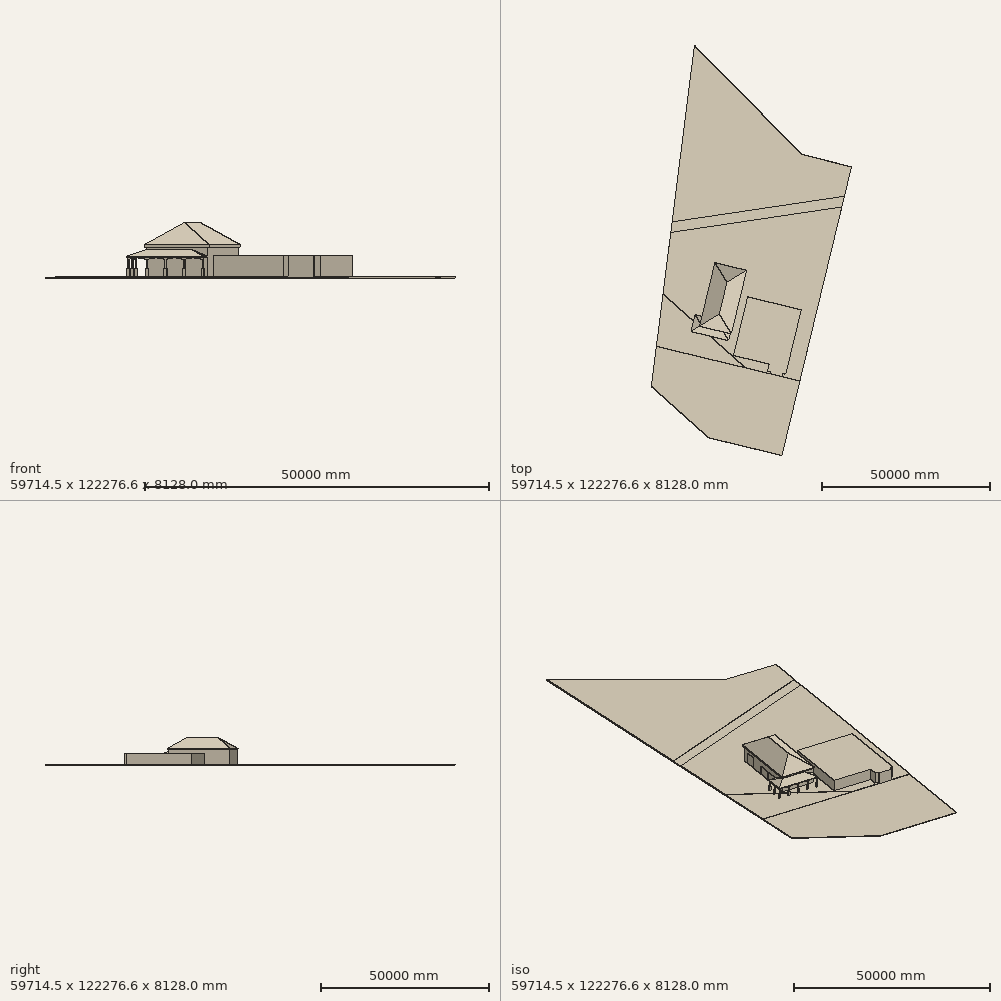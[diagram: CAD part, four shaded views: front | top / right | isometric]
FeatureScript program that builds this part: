
annotation { "Feature Type Name" : "Feature", "Feature Type Description" : "" }
export const myFeature = defineFeature(function(context is Context, id is Id, definition is map)
    precondition{}
    {
        {
            var Q0;
            Q0=qCreatedBy(makeId("Top.planeOp"),FACE);
            var sketch = newSketch(context, id + "F0", { "sketchPlane" : qUnion([Q0])});
            skLineSegment(sketch, "E0", {"start": v(0, 0) * mm, "end": v(31989.83, -32467.96) * mm});
            skLineSegment(sketch, "E1", {"start": v(31989.83, -32467.96) * mm, "end": v(46862.18, -36229.17) * mm});
            skLineSegment(sketch, "E2", {"start": v(46862.18, -36229.17) * mm, "end": v(26112.23, -122276.56) * mm});
            skLineSegment(sketch, "E3", {"start": v(46862.18, -36229.17) * mm, "end": v(46862.18, -51469.17) * mm, "construction": true});
            skLineSegment(sketch, "E4", {"start": v(0, 0) * mm, "end": v(-12852.3, -101676.89) * mm});
            skLineSegment(sketch, "E5", {"start": v(0, 0) * mm, "end": v(0, 15240) * mm, "construction": true});
            skLineSegment(sketch, "E6", {"start": v(26112.23, -122276.56) * mm, "end": v(4230, -116999.76) * mm});
            skLineSegment(sketch, "E7", {"start": v(26112.23, -122276.56) * mm, "end": v(10872.23, -122276.56) * mm, "construction": true});
            skLineSegment(sketch, "E8", {"start": v(4230, -116999.76) * mm, "end": v(-12852.3, -101676.89) * mm});
            skArc(sketch, "E9", {"start": v(-4165.07, -109469.35) * mm, "mid": v(-689.73, -114039.67) * mm, "end": v(4230, -116999.76) * mm, "construction": true});
            skArc(sketch, "E10", {"start": v(-4165.07, -109469.35) * mm, "mid": v(-8132.26, -105153.47) * mm, "end": v(-12852.3, -101676.89) * mm, "construction": true});
            skLineSegment(sketch, "E11", {"start": v(31471.2, -100053.58) * mm, "end": v(-11342.08, -89729.35) * mm});
            skLineSegment(sketch, "E12", {"start": v(-9365.85, -74095.03) * mm, "end": v(15198.72, -96129.54) * mm});
            skLineSegment(sketch, "E13", {"start": v(-6651.63, -52622.31) * mm, "end": v(44754.67, -44968.73) * mm});
            skLineSegment(sketch, "E14", {"start": v(-7048.63, -55763.02) * mm, "end": v(43983.88, -48165.09) * mm});
            skSolve(sketch);
        }
        {
            var Q0;
            {var subQ4=sQuery(id+"F0.wireOp",EDGE,"E0");Q0=makeQuery(id+"F0.imprint","IMPRINT",FACE,{"disambiguationData":[TD([[makeQuery(id+"F0.imprint","IMPRINT",EDGE,{"derivedFrom":subQ4}),-1.0]])]});}
            var Q1;
            {var subQ0=sQuery(id+"F0.wireOp",EDGE,"E13");Q1=makeQuery(id+"F0.imprint","IMPRINT",FACE,{"disambiguationData":[TD([[makeQuery(id+"F0.imprint","IMPRINT",EDGE,{"derivedFrom":subQ0}),-1.0]])]});}
            var Q2;
            {var subQ0=sQuery(id+"F0.wireOp",EDGE,"E12");Q2=makeQuery(id+"F0.imprint","IMPRINT",FACE,{"disambiguationData":[TD([[makeQuery(id+"F0.imprint","IMPRINT",EDGE,{"derivedFrom":subQ0}),1.0]])]});}
            var Q3;
            {var subQ3=sQuery(id+"F0.wireOp",EDGE,"E12");Q3=makeQuery(id+"F0.imprint","IMPRINT",FACE,{"disambiguationData":[TD([[makeQuery(id+"F0.imprint","IMPRINT",EDGE,{"derivedFrom":subQ3}),-1.0]])]});}
            var Q4;
            {var subQ1=sQuery(id+"F0.wireOp",EDGE,"E6");Q4=makeQuery(id+"F0.imprint","IMPRINT",FACE,{"disambiguationData":[TD([[makeQuery(id+"F0.imprint","IMPRINT",EDGE,{"derivedFrom":subQ1}),-1.0]])]});}
            extrude(context, id + "F1", {"entities" : qUnion([Q0, Q1, Q2, Q3, Q4]), "depth" : 304.8 * mm, "offsetDistance" : 25.4 * mm});
        }
        {
            var Q0;
            Q0=makeQuery(id+"F1.opExtrude","CAP_FACE",FACE,{"disambiguationData":[OSD([sQuery(id+"F0.wireOp",EDGE,"E0"),sQuery(id+"F0.wireOp",EDGE,"E1"),sQuery(id+"F0.wireOp",EDGE,"E2"),sQuery(id+"F0.wireOp",EDGE,"E4"),sQuery(id+"F0.wireOp",EDGE,"E6"),sQuery(id+"F0.wireOp",EDGE,"E8")])],"isStart":false});
            var sketch = newSketch(context, id + "F2", { "sketchPlane" : qUnion([Q0])});
            skLineSegment(sketch, "E15.0", {"start": v(-9365.85, -74095.03) * mm, "end": v(15198.72, -96129.54) * mm});
            skLineSegment(sketch, "E16.0", {"start": v(31471.2, -100053.58) * mm, "end": v(-11342.08, -89729.35) * mm});
            skLineSegment(sketch, "E17.0", {"start": v(0, 0) * mm, "end": v(-12852.3, -101676.89) * mm});
            skSolve(sketch);
        }
        {
            var Q0;
            {var subQ0=sQuery(id+"F2.wireOp",EDGE,"E15.0");Q0=makeQuery(id+"F2.imprint","IMPRINT",FACE,{"disambiguationData":[TD([[makeQuery(id+"F2.imprint","IMPRINT",EDGE,{"derivedFrom":subQ0}),-1.0]])]});}
            extrude(context, id + "F3", {"entities" : qUnion([Q0]), "operationType" : NewBodyOperationType.REMOVE, "oppositeDirection" : true, "depth" : 76.2 * mm, "offsetDistance" : 25.4 * mm});
        }
        {
            var Q0;
            Q0=makeQuery(id+"F1.opExtrude","CAP_FACE",FACE,{"disambiguationData":[OSD([sQuery(id+"F0.wireOp",EDGE,"E0"),sQuery(id+"F0.wireOp",EDGE,"E1"),sQuery(id+"F0.wireOp",EDGE,"E2"),sQuery(id+"F0.wireOp",EDGE,"E4"),sQuery(id+"F0.wireOp",EDGE,"E6"),sQuery(id+"F0.wireOp",EDGE,"E8")])],"isStart":false});
            var sketch = newSketch(context, id + "F4", { "sketchPlane" : qUnion([Q0])});
            skLineSegment(sketch, "E18.0", {"start": v(0, 0) * mm, "end": v(-12852.3, -101676.89) * mm});
            skLineSegment(sketch, "E19.0", {"start": v(4230, -116999.76) * mm, "end": v(-12852.3, -101676.89) * mm});
            skLineSegment(sketch, "E20.0", {"start": v(26112.23, -122276.56) * mm, "end": v(4230, -116999.76) * mm});
            skLineSegment(sketch, "E21.0", {"start": v(46862.18, -36229.17) * mm, "end": v(26112.23, -122276.56) * mm});
            skLineSegment(sketch, "E22.0", {"start": v(31471.2, -100053.58) * mm, "end": v(-11342.08, -89729.35) * mm});
            skSolve(sketch);
        }
        {
            var Q0;
            {var subQ4=sQuery(id+"F4.wireOp",EDGE,"E19.0");Q0=makeQuery(id+"F4.imprint","IMPRINT",FACE,{"disambiguationData":[TD([[makeQuery(id+"F4.imprint","IMPRINT",EDGE,{"derivedFrom":subQ4}),-1.0]])]});}
            extrude(context, id + "F5", {"entities" : qUnion([Q0]), "operationType" : NewBodyOperationType.REMOVE, "oppositeDirection" : true, "depth" : 152.4 * mm, "offsetDistance" : 25.4 * mm});
        }
        {
            var Q0;
            Q0=makeQuery(id+"F1.opExtrude","CAP_FACE",FACE,{"disambiguationData":[OSD([sQuery(id+"F0.wireOp",EDGE,"E0"),sQuery(id+"F0.wireOp",EDGE,"E1"),sQuery(id+"F0.wireOp",EDGE,"E2"),sQuery(id+"F0.wireOp",EDGE,"E4"),sQuery(id+"F0.wireOp",EDGE,"E6"),sQuery(id+"F0.wireOp",EDGE,"E8")])],"isStart":false});
            var sketch = newSketch(context, id + "F6", { "sketchPlane" : qUnion([Q0])});
            skLineSegment(sketch, "E23.0", {"start": v(-6651.63, -52622.31) * mm, "end": v(44754.67, -44968.73) * mm});
            skLineSegment(sketch, "E24.0", {"start": v(-7048.63, -55763.02) * mm, "end": v(43983.88, -48165.09) * mm});
            skLineSegment(sketch, "E25.0", {"start": v(0, 0) * mm, "end": v(-12852.3, -101676.89) * mm});
            skLineSegment(sketch, "E26.0", {"start": v(46862.18, -36229.17) * mm, "end": v(26112.23, -122276.56) * mm});
            skSolve(sketch);
        }
        {
            var Q0;
            {var subQ0=sQuery(id+"F6.wireOp",EDGE,"E23.0");Q0=makeQuery(id+"F6.imprint","IMPRINT",FACE,{"disambiguationData":[TD([[makeQuery(id+"F6.imprint","IMPRINT",EDGE,{"derivedFrom":subQ0}),-1.0]])]});}
            extrude(context, id + "F7", {"entities" : qUnion([Q0]), "operationType" : NewBodyOperationType.REMOVE, "oppositeDirection" : true, "depth" : 152.4 * mm, "offsetDistance" : 25.4 * mm});
        }
        {
            var Q0;
            {var subQ0=sQuery(id+"F0.wireOp",EDGE,"E4");var subQ1=sQuery(id+"F0.wireOp",EDGE,"E2");Q0=makeQuery(id+"F7.boolean.opBoolean","SPLIT",FACE,{"disambiguationData":[TD([makeQuery(id+"F3.boolean.opBoolean","COPY",FACE,{"derivedFrom":makeQuery(id+"F3.opExtrude","SWEPT_FACE",FACE,{"disambiguationData":[OSD([sQuery(id+"F2.wireOp",EDGE,"E15.0")])]})})])],"derivedFrom":makeQuery(id+"F1.opExtrude","CAP_FACE",FACE,{"disambiguationData":[OSD([sQuery(id+"F0.wireOp",EDGE,"E0"),sQuery(id+"F0.wireOp",EDGE,"E1"),subQ1,subQ0,sQuery(id+"F0.wireOp",EDGE,"E6"),sQuery(id+"F0.wireOp",EDGE,"E8")])],"isStart":false})});}
            var sketch = newSketch(context, id + "F8", { "sketchPlane" : qUnion([Q0])});
            skLineSegment(sketch, "E27", {"start": v(27026.6, -98981.79) * mm, "end": v(31885.4, -78832.95) * mm});
            skLineSegment(sketch, "E28", {"start": v(31885.4, -78832.95) * mm, "end": v(15884.86, -74974.49) * mm});
            skLineSegment(sketch, "E29", {"start": v(15884.86, -74974.49) * mm, "end": v(11669.13, -92456.57) * mm});
            skPoint(sketch, "E30.orphan", {"position": v(31471.2, -100053.58) * mm});
            skLineSegment(sketch, "E31.0", {"start": v(4230, -116999.76) * mm, "end": v(-12852.3, -101676.89) * mm});
            skLineSegment(sketch, "E32", {"start": v(-8757.03, -80946.6) * mm, "end": v(-11527.6, -102865.13) * mm});
            skLineSegment(sketch, "E33", {"start": v(27240.96, -98092.87) * mm, "end": v(26352.04, -97878.5) * mm});
            skLineSegment(sketch, "E34", {"start": v(26352.04, -97878.5) * mm, "end": v(26137.69, -98767.43) * mm});
            skLineSegment(sketch, "E35", {"start": v(22582, -97910) * mm, "end": v(22724.91, -97317.38) * mm});
            skLineSegment(sketch, "E36", {"start": v(22724.91, -97317.38) * mm, "end": v(21836, -97103.02) * mm});
            skLineSegment(sketch, "E37", {"start": v(21836, -97103.02) * mm, "end": v(22336.17, -95028.87) * mm});
            skLineSegment(sketch, "E38", {"start": v(11669.13, -92456.57) * mm, "end": v(22336.17, -95028.87) * mm});
            skLineSegment(sketch, "E39", {"start": v(7991.54, -94705.1) * mm, "end": v(21621.64, -97991.94) * mm});
            skLineSegment(sketch, "E40", {"start": v(21621.64, -97991.94) * mm, "end": v(21836, -97103.02) * mm});
            skLineSegment(sketch, "E41", {"start": v(19076.8, -94242.9) * mm, "end": v(18362.27, -97205.96) * mm});
            skLineSegment(sketch, "E42", {"start": v(-5179.38, -81809.34) * mm, "end": v(-8216.34, -105835.35) * mm});
            skLineSegment(sketch, "E43", {"start": v(1910, -83518.92) * mm, "end": v(6340.09, -65147.92) * mm});
            skLineSegment(sketch, "E44", {"start": v(6340.09, -65147.92) * mm, "end": v(15229.28, -67291.5) * mm});
            skLineSegment(sketch, "E45", {"start": v(15229.28, -67291.5) * mm, "end": v(10799.2, -85662.5) * mm});
            skLineSegment(sketch, "E46", {"start": v(10799.2, -85662.5) * mm, "end": v(1910, -83518.92) * mm});
            skLineSegment(sketch, "E47", {"start": v(1910, -83518.92) * mm, "end": v(-10188.29, -80601.47) * mm});
            skLineSegment(sketch, "E48", {"start": v(-8757.03, -80946.6) * mm, "end": v(-4326.94, -62575.6) * mm});
            skLineSegment(sketch, "E49", {"start": v(-4326.94, -62575.6) * mm, "end": v(6340.09, -65147.92) * mm});
            skLineSegment(sketch, "E50", {"start": v(-1032.07, -85317.74) * mm, "end": v(10227.57, -88032.96) * mm});
            skLineSegment(sketch, "E51", {"start": v(10227.57, -88032.96) * mm, "end": v(10799.2, -85662.5) * mm});
            skLineSegment(sketch, "E52", {"start": v(981.84, -31120.8) * mm, "end": v(-1311.58, -49264.42) * mm});
            skLineSegment(sketch, "E53", {"start": v(-1311.58, -49264.42) * mm, "end": v(5945.87, -50181.79) * mm});
            skLineSegment(sketch, "E54", {"start": v(5945.87, -50181.79) * mm, "end": v(8239.29, -32038.16) * mm});
            skLineSegment(sketch, "E55", {"start": v(8239.29, -32038.16) * mm, "end": v(981.84, -31120.8) * mm});
            skLineSegment(sketch, "E56", {"start": v(502.78, -49493.76) * mm, "end": v(-4326.94, -62575.6) * mm});
            skLineSegment(sketch, "E57", {"start": v(4131.51, -49952.44) * mm, "end": v(-839.37, -63416.62) * mm});
            skLineSegment(sketch, "E58", {"start": v(12240.76, -90086.11) * mm, "end": v(9277.7, -89371.58) * mm});
            skLineSegment(sketch, "E59", {"start": v(9277.7, -89371.58) * mm, "end": v(7991.54, -94705.1) * mm});
            skLineSegment(sketch, "E60", {"start": v(-460.45, -82947.3) * mm, "end": v(-1032.07, -85317.74) * mm});
            skArc(sketch, "E61", {"start": v(-10215.73, -111668.38) * mm, "mid": v(-43762.44, -101323.62) * mm, "end": v(-60941.82, -131938.4) * mm});
            skLineSegment(sketch, "E62", {"start": v(4901.73, -122178.34) * mm, "end": v(119195.03, -149739.66) * mm});
            skLineSegment(sketch, "E63", {"start": v(-12852.3, -101676.89) * mm, "end": v(-102781.45, -181077.95) * mm});
            skLineSegment(sketch, "E64", {"start": v(-60941.82, -131938.4) * mm, "end": v(-108833.54, -174223.4) * mm});
            skLineSegment(sketch, "E65", {"start": v(-108833.54, -174223.4) * mm, "end": v(-102781.45, -181077.95) * mm});
            skLineSegment(sketch, "E66", {"start": v(119195.03, -149739.66) * mm, "end": v(117051.44, -158628.86) * mm});
            skLineSegment(sketch, "E67", {"start": v(117051.44, -158628.86) * mm, "end": v(-11988.03, -127511.56) * mm});
            skArc(sketch, "E68", {"start": v(-11988.03, -127511.56) * mm, "mid": v(-34214.88, -127586.13) * mm, "end": v(-53895.9, -137915.49) * mm});
            skLineSegment(sketch, "E69", {"start": v(-53895.9, -137915.49) * mm, "end": v(-11988.03, -127511.56) * mm, "construction": true});
            skArc(sketch, "E70", {"start": v(-10215.73, -111668.38) * mm, "mid": v(-3642.82, -118341.35) * mm, "end": v(4901.73, -122178.34) * mm});
            skLineSegment(sketch, "E71", {"start": v(-69021.48, -139072.17) * mm, "end": v(-59006.2, -116101.98) * mm});
            skLineSegment(sketch, "E72", {"start": v(-11527.6, -102865.13) * mm, "end": v(-12296.94, -108951.53) * mm});
            skLineSegment(sketch, "E73", {"start": v(-8216.34, -105835.35) * mm, "end": v(-9140.66, -113147.8) * mm});
            skArc(sketch, "E74", {"start": v(-13883.76, -107269.78) * mm, "mid": v(-12418.92, -106109.18) * mm, "end": v(-11718.64, -104376.46) * mm});
            skArc(sketch, "E75", {"start": v(-8940.54, -111564.61) * mm, "mid": v(-8802.47, -113115.72) * mm, "end": v(-8031.66, -114468.8) * mm});
            skArc(sketch, "E76", {"start": v(942.8, -76557.7) * mm, "mid": v(-5172.58, -77694.5) * mm, "end": v(-8403.37, -83009.77) * mm});
            skLineSegment(sketch, "E77", {"start": v(-843.53, -83965.36) * mm, "end": v(-8403.37, -83009.77) * mm, "construction": true});
            skLineSegment(sketch, "E78", {"start": v(-8403.37, -83009.77) * mm, "end": v(-9008.16, -82933.32) * mm, "construction": true});
            skLineSegment(sketch, "E79", {"start": v(3443.26, -77160.67) * mm, "end": v(942.8, -76557.7) * mm});
            skArc(sketch, "E80", {"start": v(466.45, -78533.07) * mm, "mid": v(-4018.16, -79366.73) * mm, "end": v(-6387.41, -83264.6) * mm});
            skLineSegment(sketch, "E81", {"start": v(-6387.41, -83264.6) * mm, "end": v(-8403.37, -83009.77) * mm, "construction": true});
            skLineSegment(sketch, "E82", {"start": v(2966.91, -79136.05) * mm, "end": v(466.45, -78533.07) * mm});
            skSolve(sketch);
        }
        {
            var Q0;
            {var subQ6=sQuery(id+"F8.wireOp",EDGE,"E28");Q0=makeQuery(id+"F8.imprint","IMPRINT",FACE,{"disambiguationData":[TD([[makeQuery(id+"F8.imprint","IMPRINT",EDGE,{"derivedFrom":subQ6}),1.0]])]});}
            extrude(context, id + "F9", {"entities" : qUnion([Q0]), "operationType" : NewBodyOperationType.ADD, "depth" : 3048 * mm, "offsetDistance" : 25.4 * mm});
        }
        {
            var Q0;
            Q0=makeQuery(id+"F8.imprint","IMPRINT",FACE,{"disambiguationData":[TD([[makeQuery(id+"F8.imprint","IMPRINT",EDGE,{"derivedFrom":sQuery(id+"F8.wireOp",EDGE,"E43")}),-1.0]])]});
            extrude(context, id + "F10", {"entities" : qUnion([Q0]), "operationType" : NewBodyOperationType.ADD, "depth" : 4267.2 * mm, "offsetDistance" : 25.4 * mm});
        }
        {
            var Q0;
            Q0=makeQuery(id+"F10.opExtrude","CAP_FACE",FACE,{"disambiguationData":[OSD([sQuery(id+"F8.wireOp",EDGE,"E43"),sQuery(id+"F8.wireOp",EDGE,"E44"),sQuery(id+"F8.wireOp",EDGE,"E45"),sQuery(id+"F8.wireOp",EDGE,"E46")])],"isStart":false});
            var sketch = newSketch(context, id + "F11", { "sketchPlane" : qUnion([Q0])});
            skLineSegment(sketch, "E83.0", {"start": v(1542.24, -83743.77) * mm, "end": v(11024.05, -86030.27) * mm});
            skLineSegment(sketch, "E83.1", {"start": v(6115.23, -64780.16) * mm, "end": v(1542.24, -83743.77) * mm});
            skLineSegment(sketch, "E83.2", {"start": v(15597.04, -67066.65) * mm, "end": v(6115.23, -64780.16) * mm});
            skLineSegment(sketch, "E83.3", {"start": v(11024.05, -86030.27) * mm, "end": v(15597.04, -67066.65) * mm});
            skSolve(sketch);
        }
        {
            var Q0;
            Q0 = qSketchRegion(id + "F11", true);
            extrude(context, id + "F12", {"entities" : qUnion([Q0]), "operationType" : NewBodyOperationType.ADD, "depth" : 9144 * mm, "offsetDistance" : 25.4 * mm});
        }
        {
            var Q0;
            Q0=makeQuery(id+"F12.opExtrude","SWEPT_FACE",FACE,{"disambiguationData":[OSD([sQuery(id+"F11.wireOp",EDGE,"E83.0")])]});
            var sketch = newSketch(context, id + "F13", { "sketchPlane" : qUnion([Q0])});
            skLineSegment(sketch, "E84.0.0", {"start": v(21130.97, 4572) * mm, "end": v(30884.57, 4572) * mm});
            skLineSegment(sketch, "E84.0.1", {"start": v(30884.57, 4572) * mm, "end": v(30884.57, 13716) * mm});
            skLineSegment(sketch, "E84.0.2", {"start": v(30884.57, 13716) * mm, "end": v(21130.97, 13716) * mm});
            skLineSegment(sketch, "E84.0.3", {"start": v(21130.97, 13716) * mm, "end": v(21130.97, 4572) * mm});
            skLineSegment(sketch, "E85", {"start": v(21130.97, 4876.8) * mm, "end": v(26007.77, 8128) * mm});
            skLineSegment(sketch, "E86", {"start": v(26007.77, 8128) * mm, "end": v(30884.57, 4876.8) * mm});
            skLineSegment(sketch, "E87", {"start": v(21130.97, 4876.8) * mm, "end": v(21435.77, 4876.8) * mm, "construction": true});
            skLineSegment(sketch, "E88", {"start": v(21435.77, 4876.8) * mm, "end": v(21435.77, 5080) * mm, "construction": true});
            skSolve(sketch);
        }
        {
            var Q0;
            {var subQ1=sQuery(id+"F13.wireOp",EDGE,"E84.0.2");Q0=makeQuery(id+"F13.imprint","IMPRINT",FACE,{"disambiguationData":[TD([[makeQuery(id+"F13.imprint","IMPRINT",EDGE,{"derivedFrom":subQ1}),-1.0]])]});}
            extrude(context, id + "F14", {"entities" : qUnion([Q0]), "operationType" : NewBodyOperationType.REMOVE, "endBound" : BoundingType.THROUGH_ALL, "oppositeDirection" : true, "depth" : 25.4 * mm, "offsetDistance" : 25.4 * mm});
        }
        {
            var Q0;
            Q0=makeQuery(id+"F12.opExtrude","SWEPT_FACE",FACE,{"disambiguationData":[OSD([sQuery(id+"F11.wireOp",EDGE,"E83.1")])]});
            var sketch = newSketch(context, id + "F15", { "sketchPlane" : qUnion([Q0])});
            skLineSegment(sketch, "E89.0.0", {"start": v(61541.43, 4876.8) * mm, "end": v(81048.63, 4876.8) * mm});
            skLineSegment(sketch, "E89.0.1", {"start": v(81048.63, 4876.8) * mm, "end": v(81048.63, 8128) * mm});
            skLineSegment(sketch, "E89.0.2", {"start": v(81048.63, 8128) * mm, "end": v(61541.43, 8128) * mm});
            skLineSegment(sketch, "E89.0.3", {"start": v(61541.43, 8128) * mm, "end": v(61541.43, 4876.8) * mm});
            skLineSegment(sketch, "E90", {"start": v(61541.43, 4876.8) * mm, "end": v(66418.23, 8128) * mm});
            skLineSegment(sketch, "E91", {"start": v(81048.63, 4876.8) * mm, "end": v(76171.83, 8128) * mm});
            skLineSegment(sketch, "E92", {"start": v(61846.23, 5080) * mm, "end": v(61846.23, 4876.8) * mm, "construction": true});
            skSolve(sketch);
        }
        {
            var Q0;
            {var subQ0=sQuery(id+"F15.wireOp",EDGE,"E89.0.3");Q0=makeQuery(id+"F15.imprint","IMPRINT",FACE,{"disambiguationData":[TD([[makeQuery(id+"F15.imprint","IMPRINT",EDGE,{"derivedFrom":subQ0}),1.0]])]});}
            var Q1;
            {var subQ0=sQuery(id+"F15.wireOp",EDGE,"E89.0.1");Q1=makeQuery(id+"F15.imprint","IMPRINT",FACE,{"disambiguationData":[TD([[makeQuery(id+"F15.imprint","IMPRINT",EDGE,{"derivedFrom":subQ0}),1.0]])]});}
            extrude(context, id + "F16", {"entities" : qUnion([Q0, Q1]), "operationType" : NewBodyOperationType.REMOVE, "endBound" : BoundingType.THROUGH_ALL, "oppositeDirection" : true, "depth" : 25.4 * mm, "offsetDistance" : 25.4 * mm});
        }
        {
            var Q0;
            Q0=makeQuery(id+"F10.opExtrude","SWEPT_FACE",FACE,{"disambiguationData":[OSD([sQuery(id+"F8.wireOp",EDGE,"E46")])]});
            var sketch = newSketch(context, id + "F17", { "sketchPlane" : qUnion([Q0])});
            skLineSegment(sketch, "E93.0.0", {"start": v(21435.77, 304.8) * mm, "end": v(30579.77, 304.8) * mm});
            skLineSegment(sketch, "E93.0.1", {"start": v(30579.77, 304.8) * mm, "end": v(30579.77, 4572) * mm});
            skLineSegment(sketch, "E93.0.2", {"start": v(30579.77, 4572) * mm, "end": v(21435.77, 4572) * mm});
            skLineSegment(sketch, "E93.0.3", {"start": v(21435.77, 4572) * mm, "end": v(21435.77, 304.8) * mm});
            skLineSegment(sketch, "E94", {"start": v(30579.77, 3048) * mm, "end": v(18997.37, 3048) * mm});
            skLineSegment(sketch, "E95", {"start": v(18997.37, 3048) * mm, "end": v(18997.37, 3200.4) * mm});
            skLineSegment(sketch, "E96", {"start": v(18997.37, 3200.4) * mm, "end": v(21435.77, 4216.4) * mm});
            skLineSegment(sketch, "E97", {"start": v(21435.77, 4216.4) * mm, "end": v(28141.37, 4216.4) * mm});
            skLineSegment(sketch, "E98", {"start": v(28141.37, 4216.4) * mm, "end": v(30579.77, 3200.4) * mm});
            skLineSegment(sketch, "E99", {"start": v(30579.77, 3200.4) * mm, "end": v(30579.77, 3048) * mm});
            skLineSegment(sketch, "E100", {"start": v(18997.37, 3200.4) * mm, "end": v(19302.17, 3200.4) * mm, "construction": true});
            skLineSegment(sketch, "E101", {"start": v(19302.17, 3200.4) * mm, "end": v(19302.17, 3327.4) * mm, "construction": true});
            skSolve(sketch);
        }
        {
            var Q0;
            {var subQ4=sQuery(id+"F17.wireOp",EDGE,"E95");Q0=makeQuery(id+"F17.imprint","IMPRINT",FACE,{"disambiguationData":[TD([[makeQuery(id+"F17.imprint","IMPRINT",EDGE,{"derivedFrom":subQ4}),-1.0]])]});}
            var Q1;
            {var subQ5=sQuery(id+"F17.wireOp",EDGE,"E97");Q1=makeQuery(id+"F17.imprint","IMPRINT",FACE,{"disambiguationData":[TD([[makeQuery(id+"F17.imprint","IMPRINT",EDGE,{"derivedFrom":subQ5}),-1.0]])]});}
            extrude(context, id + "F18", {"entities" : qUnion([Q0, Q1]), "operationType" : NewBodyOperationType.ADD, "depth" : 2438.4 * mm, "offsetDistance" : 25.4 * mm, "hasSecondDirection" : true, "secondDirectionOppositeDirection" : true, "secondDirectionDepth" : 2743.2 * mm});
        }
        {
            var Q0;
            Q0=makeQuery(id+"F18.opExtrude","SWEPT_FACE",FACE,{"disambiguationData":[OSD([sQuery(id+"F17.wireOp",EDGE,"E95")])]});
            var sketch = newSketch(context, id + "F19", { "sketchPlane" : qUnion([Q0])});
            skLineSegment(sketch, "E102.0.0", {"start": v(78000.63, 4216.4) * mm, "end": v(78000.63, 3200.4) * mm});
            skLineSegment(sketch, "E102.0.1", {"start": v(78000.63, 3200.4) * mm, "end": v(83182.23, 3200.4) * mm});
            skLineSegment(sketch, "E102.0.2", {"start": v(83182.23, 3200.4) * mm, "end": v(83182.23, 4216.4) * mm});
            skLineSegment(sketch, "E102.0.3", {"start": v(83182.23, 4216.4) * mm, "end": v(80743.83, 4216.4) * mm});
            skLineSegment(sketch, "E102.0.4", {"start": v(80743.83, 4216.4) * mm, "end": v(78000.63, 4216.4) * mm});
            skLineSegment(sketch, "E103", {"start": v(80743.83, 4216.4) * mm, "end": v(83182.23, 3200.4) * mm});
            skLineSegment(sketch, "E104", {"start": v(78000.63, 3200.4) * mm, "end": v(80439.03, 4216.4) * mm});
            skSolve(sketch);
        }
        {
            var Q0;
            Q0=makeQuery(id+"F19.imprint","IMPRINT",FACE,{"disambiguationData":[TD([[makeQuery(id+"F19.imprint","IMPRINT",EDGE,{"derivedFrom":sQuery(id+"F19.wireOp",EDGE,"E102.0.2")}),1.0]])]});
            var Q1;
            Q1=makeQuery(id+"F18.boolean.opBoolean","MERGE",FACE,{"derivedFrom":[makeQuery(id+"F10.opExtrude","SWEPT_FACE",FACE,{"disambiguationData":[OSD([sQuery(id+"F8.wireOp",EDGE,"E45")])]}),makeQuery(id+"F18.opExtrude","SWEPT_FACE",FACE,{"disambiguationData":[OSD([sQuery(id+"F17.wireOp",EDGE,"E93.0.1")])]})]});
            extrude(context, id + "F20", {"entities" : qUnion([Q0]), "operationType" : NewBodyOperationType.REMOVE, "endBound" : BoundingType.UP_TO_SURFACE, "oppositeDirection" : true, "depth" : 25.4 * mm, "endBoundEntityFace" : qUnion([Q1]), "offsetDistance" : 25.4 * mm});
        }
        {
            var Q0;
            {var subQ0=sQuery(id+"F19.wireOp",EDGE,"E102.0.0");Q0=makeQuery(id+"F19.imprint","IMPRINT",FACE,{"disambiguationData":[TD([[makeQuery(id+"F19.imprint","IMPRINT",EDGE,{"derivedFrom":subQ0}),1.0]])]});}
            var Q1;
            Q1=makeQuery(id+"F10.opExtrude","SWEPT_FACE",FACE,{"disambiguationData":[OSD([sQuery(id+"F8.wireOp",EDGE,"E43")])]});
            extrude(context, id + "F21", {"entities" : qUnion([Q0]), "operationType" : NewBodyOperationType.REMOVE, "endBound" : BoundingType.UP_TO_SURFACE, "oppositeDirection" : true, "depth" : 25.4 * mm, "endBoundEntityFace" : qUnion([Q1]), "offsetDistance" : 25.4 * mm});
        }
        {
            var Q0;
            Q0=makeQuery(id+"F3.boolean.opBoolean","COPY",FACE,{"derivedFrom":makeQuery(id+"F3.opExtrude","CAP_FACE",FACE,{"disambiguationData":[OSD([sQuery(id+"F2.wireOp",EDGE,"E15.0"),sQuery(id+"F2.wireOp",EDGE,"E16.0"),sQuery(id+"F2.wireOp",EDGE,"E17.0")])],"isStart":false})});
            var sketch = newSketch(context, id + "F22", { "sketchPlane" : qUnion([Q0])});
            skLineSegment(sketch, "E105.0.0", {"start": v(2553.08, -80852.16) * mm, "end": v(1910, -83518.92) * mm});
            skLineSegment(sketch, "E105.0.1", {"start": v(1910, -83518.92) * mm, "end": v(10799.2, -85662.5) * mm});
            skLineSegment(sketch, "E105.0.2", {"start": v(10799.2, -85662.5) * mm, "end": v(10227.57, -88032.96) * mm});
            skLineSegment(sketch, "E105.0.3", {"start": v(10227.57, -88032.96) * mm, "end": v(-1032.07, -85317.74) * mm});
            skLineSegment(sketch, "E105.0.4", {"start": v(-1032.07, -85317.74) * mm, "end": v(182.63, -80280.53) * mm});
            skLineSegment(sketch, "E105.0.5", {"start": v(182.63, -80280.53) * mm, "end": v(2553.08, -80852.16) * mm});
            skLineSegment(sketch, "E106", {"start": v(-936.8, -84922.67) * mm, "end": v(-541.73, -85017.94) * mm});
            skLineSegment(sketch, "E107", {"start": v(577.7, -80375.8) * mm, "end": v(482.43, -80770.88) * mm});
            skLineSegment(sketch, "E108", {"start": v(87.36, -80675.61) * mm, "end": v(482.43, -80770.88) * mm});
            skLineSegment(sketch, "E109", {"start": v(9927.77, -87542.61) * mm, "end": v(9832.5, -87937.69) * mm});
            skLineSegment(sketch, "E110", {"start": v(1779.34, -85577.65) * mm, "end": v(1684.07, -85972.73) * mm});
            skLineSegment(sketch, "E111", {"start": v(2174.41, -85672.93) * mm, "end": v(2079.14, -86068) * mm});
            skLineSegment(sketch, "E112", {"start": v(4495.48, -86232.64) * mm, "end": v(4400.21, -86627.72) * mm});
            skLineSegment(sketch, "E113", {"start": v(4890.56, -86327.91) * mm, "end": v(4795.29, -86722.99) * mm});
            skLineSegment(sketch, "E114", {"start": v(7211.62, -86887.63) * mm, "end": v(7116.35, -87282.7) * mm});
            skLineSegment(sketch, "E115", {"start": v(7606.7, -86982.9) * mm, "end": v(7511.43, -87377.97) * mm});
            skLineSegment(sketch, "E116", {"start": v(-541.73, -85017.94) * mm, "end": v(1779.34, -85577.65) * mm});
            skLineSegment(sketch, "E117", {"start": v(1779.34, -85577.65) * mm, "end": v(2174.41, -85672.93) * mm});
            skLineSegment(sketch, "E118", {"start": v(2174.41, -85672.93) * mm, "end": v(4495.48, -86232.64) * mm});
            skLineSegment(sketch, "E119", {"start": v(4495.48, -86232.64) * mm, "end": v(4890.56, -86327.91) * mm});
            skLineSegment(sketch, "E120", {"start": v(4890.56, -86327.91) * mm, "end": v(7211.62, -86887.63) * mm});
            skLineSegment(sketch, "E121", {"start": v(7211.62, -86887.63) * mm, "end": v(7606.7, -86982.9) * mm});
            skLineSegment(sketch, "E122", {"start": v(7606.7, -86982.9) * mm, "end": v(9927.77, -87542.61) * mm});
            skLineSegment(sketch, "E123", {"start": v(9927.77, -87542.61) * mm, "end": v(10322.84, -87637.88) * mm});
            skLineSegment(sketch, "E124", {"start": v(-460.45, -82947.3) * mm, "end": v(-65.37, -83042.56) * mm});
            skLineSegment(sketch, "E125", {"start": v(-365.18, -82552.22) * mm, "end": v(29.9, -82647.49) * mm});
            skLineSegment(sketch, "E126", {"start": v(-65.37, -83042.56) * mm, "end": v(-541.73, -85017.94) * mm});
            skLineSegment(sketch, "E127", {"start": v(29.9, -82647.49) * mm, "end": v(-65.37, -83042.56) * mm});
            skLineSegment(sketch, "E128", {"start": v(-541.73, -85017.94) * mm, "end": v(-637, -85413.02) * mm});
            skLineSegment(sketch, "E129", {"start": v(482.43, -80770.88) * mm, "end": v(29.9, -82647.49) * mm});
            skSolve(sketch);
        }
        {
            var Q0;
            {var subQ4=sQuery(id+"F22.wireOp",EDGE,"E106");Q0=makeQuery(id+"F22.imprint","IMPRINT",FACE,{"disambiguationData":[TD([[makeQuery(id+"F22.imprint","IMPRINT",EDGE,{"derivedFrom":subQ4}),-1.0]])]});}
            var Q1;
            {var subQ0=sQuery(id+"F22.wireOp",EDGE,"E124");Q1=makeQuery(id+"F22.imprint","IMPRINT",FACE,{"disambiguationData":[TD([[makeQuery(id+"F22.imprint","IMPRINT",EDGE,{"derivedFrom":subQ0}),1.0]])]});}
            var Q2;
            {var subQ4=sQuery(id+"F22.wireOp",EDGE,"E107");Q2=makeQuery(id+"F22.imprint","IMPRINT",FACE,{"disambiguationData":[TD([[makeQuery(id+"F22.imprint","IMPRINT",EDGE,{"derivedFrom":subQ4}),-1.0]])]});}
            var Q3;
            {var subQ0=sQuery(id+"F22.wireOp",EDGE,"E110");Q3=makeQuery(id+"F22.imprint","IMPRINT",FACE,{"disambiguationData":[TD([[makeQuery(id+"F22.imprint","IMPRINT",EDGE,{"derivedFrom":subQ0}),1.0]])]});}
            var Q4;
            {var subQ0=sQuery(id+"F22.wireOp",EDGE,"E112");var subQ1=sQuery(id+"F22.wireOp",EDGE,"E105.0.3");var subQ2=makeQuery(id+"F22.imprint","INTERSECT",VERTEX,{"derivedFrom":[subQ1,subQ0]});Q4=makeQuery(id+"F22.imprint","IMPRINT",FACE,{"disambiguationData":[TD([[makeQuery(id+"F22.imprint","IMPRINT",EDGE,{"disambiguationData":[TD([[subQ2,1.0]])],"derivedFrom":subQ1}),-1.0]])]});}
            var Q5;
            {var subQ1=sQuery(id+"F22.wireOp",EDGE,"E113");Q5=makeQuery(id+"F22.imprint","IMPRINT",FACE,{"disambiguationData":[TD([[makeQuery(id+"F22.imprint","IMPRINT",EDGE,{"derivedFrom":subQ1}),-1.0]])]});}
            var Q6;
            {var subQ0=sQuery(id+"F22.wireOp",EDGE,"E114");Q6=makeQuery(id+"F22.imprint","IMPRINT",FACE,{"disambiguationData":[TD([[makeQuery(id+"F22.imprint","IMPRINT",EDGE,{"derivedFrom":subQ0}),1.0]])]});}
            var Q7;
            {var subQ4=sQuery(id+"F22.wireOp",EDGE,"E109");Q7=makeQuery(id+"F22.imprint","IMPRINT",FACE,{"disambiguationData":[TD([[makeQuery(id+"F22.imprint","IMPRINT",EDGE,{"derivedFrom":subQ4}),1.0]])]});}
            extrude(context, id + "F23", {"entities" : qUnion([Q0, Q1, Q2, Q3, Q4, Q5, Q6, Q7]), "operationType" : NewBodyOperationType.ADD, "depth" : 1219.2 * mm, "offsetDistance" : 25.4 * mm});
        }
        {
            var Q0;
            Q0=makeQuery(id+"F23.opExtrude","CAP_FACE",FACE,{"disambiguationData":[OSD([sQuery(id+"F22.wireOp",EDGE,"E105.0.3"),sQuery(id+"F22.wireOp",EDGE,"E105.0.4"),sQuery(id+"F22.wireOp",EDGE,"E106"),sQuery(id+"F22.wireOp",EDGE,"E128")])],"isStart":false});
            var sketch = newSketch(context, id + "F24", { "sketchPlane" : qUnion([Q0])});
            skLineSegment(sketch, "E130.0", {"start": v(-711.95, -85290.43) * mm, "end": v(-664.31, -85092.9) * mm});
            skLineSegment(sketch, "E130.1", {"start": v(-909.49, -85242.8) * mm, "end": v(-711.95, -85290.43) * mm});
            skLineSegment(sketch, "E130.2", {"start": v(-861.85, -85045.26) * mm, "end": v(-909.49, -85242.8) * mm});
            skLineSegment(sketch, "E130.3", {"start": v(-664.31, -85092.9) * mm, "end": v(-861.85, -85045.26) * mm});
            skLineSegment(sketch, "E131.0", {"start": v(-140.33, -82919.98) * mm, "end": v(-92.7, -82722.44) * mm});
            skLineSegment(sketch, "E131.1", {"start": v(-337.86, -82872.34) * mm, "end": v(-140.33, -82919.98) * mm});
            skLineSegment(sketch, "E131.2", {"start": v(-290.23, -82674.8) * mm, "end": v(-337.86, -82872.34) * mm});
            skLineSegment(sketch, "E131.3", {"start": v(-92.7, -82722.44) * mm, "end": v(-290.23, -82674.8) * mm});
            skLineSegment(sketch, "E132.0", {"start": v(257.58, -80403.12) * mm, "end": v(209.94, -80600.66) * mm});
            skLineSegment(sketch, "E132.1", {"start": v(455.12, -80450.76) * mm, "end": v(257.58, -80403.12) * mm});
            skLineSegment(sketch, "E132.2", {"start": v(407.48, -80648.3) * mm, "end": v(455.12, -80450.76) * mm});
            skLineSegment(sketch, "E132.3", {"start": v(209.94, -80600.66) * mm, "end": v(407.48, -80648.3) * mm});
            skLineSegment(sketch, "E133.0", {"start": v(2004.2, -85945.41) * mm, "end": v(2051.83, -85747.88) * mm});
            skLineSegment(sketch, "E133.1", {"start": v(1806.66, -85897.78) * mm, "end": v(2004.2, -85945.41) * mm});
            skLineSegment(sketch, "E133.2", {"start": v(1854.3, -85700.24) * mm, "end": v(1806.66, -85897.78) * mm});
            skLineSegment(sketch, "E133.3", {"start": v(2051.83, -85747.88) * mm, "end": v(1854.3, -85700.24) * mm});
            skLineSegment(sketch, "E134.0", {"start": v(4522.8, -86552.76) * mm, "end": v(4720.34, -86600.4) * mm});
            skLineSegment(sketch, "E134.1", {"start": v(4570.43, -86355.23) * mm, "end": v(4522.8, -86552.76) * mm});
            skLineSegment(sketch, "E134.2", {"start": v(4767.97, -86402.86) * mm, "end": v(4570.43, -86355.23) * mm});
            skLineSegment(sketch, "E134.3", {"start": v(4720.34, -86600.4) * mm, "end": v(4767.97, -86402.86) * mm});
            skLineSegment(sketch, "E135.0", {"start": v(7238.94, -87207.75) * mm, "end": v(7436.48, -87255.39) * mm});
            skLineSegment(sketch, "E135.1", {"start": v(7286.58, -87010.21) * mm, "end": v(7238.94, -87207.75) * mm});
            skLineSegment(sketch, "E135.2", {"start": v(7484.11, -87057.85) * mm, "end": v(7286.58, -87010.21) * mm});
            skLineSegment(sketch, "E135.3", {"start": v(7436.48, -87255.39) * mm, "end": v(7484.11, -87057.85) * mm});
            skLineSegment(sketch, "E136.0", {"start": v(9955.08, -87862.74) * mm, "end": v(10152.62, -87910.37) * mm});
            skLineSegment(sketch, "E136.1", {"start": v(10002.72, -87665.2) * mm, "end": v(9955.08, -87862.74) * mm});
            skLineSegment(sketch, "E136.2", {"start": v(10200.26, -87712.83) * mm, "end": v(10002.72, -87665.2) * mm});
            skLineSegment(sketch, "E136.3", {"start": v(10152.62, -87910.37) * mm, "end": v(10200.26, -87712.83) * mm});
            skSolve(sketch);
        }
        {
            var Q0;
            Q0 = qSketchRegion(id + "F24", true);
            var Q1;
            Q1=makeQuery(id+"F18.opExtrude","SWEPT_FACE",FACE,{"disambiguationData":[OSD([sQuery(id+"F17.wireOp",EDGE,"E94")])]});
            extrude(context, id + "F25", {"entities" : qUnion([Q0]), "operationType" : NewBodyOperationType.ADD, "endBound" : BoundingType.UP_TO_SURFACE, "depth" : 25.4 * mm, "endBoundEntityFace" : qUnion([Q1]), "offsetDistance" : 25.4 * mm});
        }
        {
            var Q0;
            Q0=makeQuery(id+"F25.opExtrude","SWEPT_FACE",FACE,{"disambiguationData":[OSD([sQuery(id+"F24.wireOp",EDGE,"E130.1")])]});
            var sketch = newSketch(context, id + "F26", { "sketchPlane" : qUnion([Q0])});
            skLineSegment(sketch, "E137.0", {"start": v(30579.77, 3048) * mm, "end": v(18997.37, 3048) * mm});
            skLineSegment(sketch, "E138.0.0", {"start": v(19302.17, 1447.8) * mm, "end": v(19302.17, 3048) * mm});
            skLineSegment(sketch, "E138.0.1", {"start": v(19302.17, 3048) * mm, "end": v(19098.97, 3048) * mm});
            skLineSegment(sketch, "E138.0.2", {"start": v(19098.97, 3048) * mm, "end": v(19098.97, 1447.8) * mm});
            skLineSegment(sketch, "E138.0.3", {"start": v(19098.97, 1447.8) * mm, "end": v(19302.17, 1447.8) * mm});
            skLineSegment(sketch, "E139.0.0", {"start": v(22096.17, 1447.8) * mm, "end": v(22096.17, 3048) * mm});
            skLineSegment(sketch, "E139.0.1", {"start": v(22096.17, 3048) * mm, "end": v(21892.97, 3048) * mm});
            skLineSegment(sketch, "E139.0.2", {"start": v(21892.97, 3048) * mm, "end": v(21892.97, 1447.8) * mm});
            skLineSegment(sketch, "E139.0.3", {"start": v(21892.97, 1447.8) * mm, "end": v(22096.17, 1447.8) * mm});
            skLineSegment(sketch, "E140.0.0", {"start": v(24890.17, 1447.8) * mm, "end": v(24890.17, 3048) * mm});
            skLineSegment(sketch, "E140.0.1", {"start": v(24890.17, 3048) * mm, "end": v(24686.97, 3048) * mm});
            skLineSegment(sketch, "E140.0.2", {"start": v(24686.97, 3048) * mm, "end": v(24686.97, 1447.8) * mm});
            skLineSegment(sketch, "E140.0.3", {"start": v(24686.97, 1447.8) * mm, "end": v(24890.17, 1447.8) * mm});
            skLineSegment(sketch, "E141.0.0", {"start": v(27684.17, 1447.8) * mm, "end": v(27684.17, 3048) * mm});
            skLineSegment(sketch, "E141.0.1", {"start": v(27684.17, 3048) * mm, "end": v(27480.97, 3048) * mm});
            skLineSegment(sketch, "E141.0.2", {"start": v(27480.97, 3048) * mm, "end": v(27480.97, 1447.8) * mm});
            skLineSegment(sketch, "E141.0.3", {"start": v(27480.97, 1447.8) * mm, "end": v(27684.17, 1447.8) * mm});
            skLineSegment(sketch, "E142.0.0", {"start": v(30478.17, 1447.8) * mm, "end": v(30478.17, 3048) * mm});
            skLineSegment(sketch, "E142.0.1", {"start": v(30478.17, 3048) * mm, "end": v(30274.97, 3048) * mm});
            skLineSegment(sketch, "E142.0.2", {"start": v(30274.97, 3048) * mm, "end": v(30274.97, 1447.8) * mm});
            skLineSegment(sketch, "E142.0.3", {"start": v(30274.97, 1447.8) * mm, "end": v(30478.17, 1447.8) * mm});
            skArc(sketch, "E143", {"start": v(21892.97, 2743.2) * mm, "mid": v(20597.57, 2980.28) * mm, "end": v(19302.17, 2743.2) * mm});
            skLineSegment(sketch, "E144", {"start": v(19302.17, 2743.2) * mm, "end": v(30274.97, 2743.2) * mm, "construction": true});
            skArc(sketch, "E145", {"start": v(24686.97, 2743.2) * mm, "mid": v(23391.57, 2980.28) * mm, "end": v(22096.17, 2743.2) * mm});
            skArc(sketch, "E146", {"start": v(27480.97, 2743.2) * mm, "mid": v(26185.57, 2980.28) * mm, "end": v(24890.17, 2743.2) * mm});
            skArc(sketch, "E147", {"start": v(30274.97, 2743.2) * mm, "mid": v(28979.57, 2980.28) * mm, "end": v(27684.17, 2743.2) * mm});
            skSolve(sketch);
        }
        {
            var Q0;
            {var subQ5=sQuery(id+"F26.wireOp",EDGE,"E143");Q0=makeQuery(id+"F26.imprint","IMPRINT",FACE,{"disambiguationData":[TD([[makeQuery(id+"F26.imprint","IMPRINT",EDGE,{"derivedFrom":subQ5}),-1.0]])]});}
            var Q1;
            {var subQ5=sQuery(id+"F26.wireOp",EDGE,"E145");Q1=makeQuery(id+"F26.imprint","IMPRINT",FACE,{"disambiguationData":[TD([[makeQuery(id+"F26.imprint","IMPRINT",EDGE,{"derivedFrom":subQ5}),-1.0]])]});}
            var Q2;
            {var subQ5=sQuery(id+"F26.wireOp",EDGE,"E146");Q2=makeQuery(id+"F26.imprint","IMPRINT",FACE,{"disambiguationData":[TD([[makeQuery(id+"F26.imprint","IMPRINT",EDGE,{"derivedFrom":subQ5}),-1.0]])]});}
            var Q3;
            {var subQ5=sQuery(id+"F26.wireOp",EDGE,"E147");Q3=makeQuery(id+"F26.imprint","IMPRINT",FACE,{"disambiguationData":[TD([[makeQuery(id+"F26.imprint","IMPRINT",EDGE,{"derivedFrom":subQ5}),-1.0]])]});}
            var Q4;
            Q4=makeQuery(id+"F25.opExtrude","SWEPT_FACE",FACE,{"disambiguationData":[OSD([sQuery(id+"F24.wireOp",EDGE,"E130.3")])]});
            extrude(context, id + "F27", {"entities" : qUnion([Q0, Q1, Q2, Q3]), "operationType" : NewBodyOperationType.ADD, "endBound" : BoundingType.UP_TO_SURFACE, "oppositeDirection" : true, "depth" : 25.4 * mm, "endBoundEntityFace" : qUnion([Q4]), "offsetDistance" : 25.4 * mm});
        }
        {
            var Q0;
            Q0=makeQuery(id+"F25.opExtrude","SWEPT_FACE",FACE,{"disambiguationData":[OSD([sQuery(id+"F24.wireOp",EDGE,"E132.0")])]});
            var sketch = newSketch(context, id + "F28", { "sketchPlane" : qUnion([Q0])});
            skLineSegment(sketch, "E148.0.0", {"start": v(78305.43, 1447.8) * mm, "end": v(78305.43, 3048) * mm});
            skLineSegment(sketch, "E148.0.1", {"start": v(78305.43, 3048) * mm, "end": v(78102.23, 3048) * mm});
            skLineSegment(sketch, "E148.0.2", {"start": v(78102.23, 3048) * mm, "end": v(78102.23, 1447.8) * mm});
            skLineSegment(sketch, "E148.0.3", {"start": v(78102.23, 1447.8) * mm, "end": v(78305.43, 1447.8) * mm});
            skLineSegment(sketch, "E149.0.0", {"start": v(80642.23, 1447.8) * mm, "end": v(80642.23, 3048) * mm});
            skLineSegment(sketch, "E149.0.1", {"start": v(80642.23, 3048) * mm, "end": v(80439.03, 3048) * mm});
            skLineSegment(sketch, "E149.0.2", {"start": v(80439.03, 3048) * mm, "end": v(80439.03, 1447.8) * mm});
            skLineSegment(sketch, "E149.0.3", {"start": v(80439.03, 1447.8) * mm, "end": v(80642.23, 1447.8) * mm});
            skLineSegment(sketch, "E150.0.0", {"start": v(83080.63, 1447.8) * mm, "end": v(83080.63, 3048) * mm});
            skLineSegment(sketch, "E150.0.1", {"start": v(83080.63, 3048) * mm, "end": v(82877.43, 3048) * mm});
            skLineSegment(sketch, "E150.0.2", {"start": v(82877.43, 3048) * mm, "end": v(82877.43, 1447.8) * mm});
            skLineSegment(sketch, "E150.0.3", {"start": v(82877.43, 1447.8) * mm, "end": v(83080.63, 1447.8) * mm});
            skLineSegment(sketch, "E151.0", {"start": v(83182.23, 3048) * mm, "end": v(78000.63, 3048) * mm});
            skLineSegment(sketch, "E152", {"start": v(78305.43, 2743.2) * mm, "end": v(82877.43, 2743.2) * mm, "construction": true});
            skArc(sketch, "E153", {"start": v(80439.03, 2743.2) * mm, "mid": v(79372.23, 2980.28) * mm, "end": v(78305.43, 2743.2) * mm});
            skArc(sketch, "E154", {"start": v(82877.43, 2743.2) * mm, "mid": v(81759.83, 2980.28) * mm, "end": v(80642.23, 2743.2) * mm});
            skPoint(sketch, "E154.endSnap0", {"position": v(80591.43, 2743.2) * mm});
            skLineSegment(sketch, "E155.0", {"start": v(83080.63, 2743.2) * mm, "end": v(83080.63, 2980.28) * mm});
            skLineSegment(sketch, "E156", {"start": v(83080.63, 2980.28) * mm, "end": v(78305.43, 2980.28) * mm, "construction": true});
            skSolve(sketch);
        }
        {
            var Q0;
            {var subQ3=sQuery(id+"F28.wireOp",EDGE,"E153");Q0=makeQuery(id+"F28.imprint","IMPRINT",FACE,{"disambiguationData":[TD([[makeQuery(id+"F28.imprint","IMPRINT",EDGE,{"derivedFrom":subQ3}),-1.0]])]});}
            var Q1;
            {var subQ3=sQuery(id+"F28.wireOp",EDGE,"E154");Q1=makeQuery(id+"F28.imprint","IMPRINT",FACE,{"disambiguationData":[TD([[makeQuery(id+"F28.imprint","IMPRINT",EDGE,{"derivedFrom":subQ3}),-1.0]])]});}
            var Q2;
            Q2=makeQuery(id+"F25.opExtrude","SWEPT_FACE",FACE,{"disambiguationData":[OSD([sQuery(id+"F24.wireOp",EDGE,"E130.0")])]});
            extrude(context, id + "F29", {"entities" : qUnion([Q0, Q1]), "operationType" : NewBodyOperationType.ADD, "endBound" : BoundingType.UP_TO_SURFACE, "oppositeDirection" : true, "depth" : 25.4 * mm, "endBoundEntityFace" : qUnion([Q2]), "offsetDistance" : 25.4 * mm});
        }
        {
            var Q0;
            Q0=makeQuery(id+"F21.boolean.opBoolean","MERGE",FACE,{"derivedFrom":[makeQuery(id+"F10.opExtrude","SWEPT_FACE",FACE,{"disambiguationData":[OSD([sQuery(id+"F8.wireOp",EDGE,"E43")])]})],"fromTools":[makeQuery(id+"F21.opExtrude","CAP_FACE",FACE,{"disambiguationData":[OSD([sQuery(id+"F19.wireOp",EDGE,"E102.0.0"),sQuery(id+"F19.wireOp",EDGE,"E102.0.4"),sQuery(id+"F19.wireOp",EDGE,"E104")])],"isStart":false})]});
            var sketch = newSketch(context, id + "F30", { "sketchPlane" : qUnion([Q0])});
            skLineSegment(sketch, "E157.0.0", {"start": v(80743.83, 3048) * mm, "end": v(78000.63, 3048) * mm});
            skLineSegment(sketch, "E157.0.1", {"start": v(78000.63, 3048) * mm, "end": v(78000.63, 3200.4) * mm});
            skLineSegment(sketch, "E157.0.2", {"start": v(78000.63, 3200.4) * mm, "end": v(80439.03, 4216.4) * mm});
            skLineSegment(sketch, "E157.0.3", {"start": v(80439.03, 4216.4) * mm, "end": v(80743.83, 4216.4) * mm});
            skLineSegment(sketch, "E157.0.4", {"start": v(80743.83, 4216.4) * mm, "end": v(80743.83, 4572) * mm});
            skLineSegment(sketch, "E157.0.5", {"start": v(80743.83, 4572) * mm, "end": v(61846.23, 4572) * mm});
            skLineSegment(sketch, "E157.0.6", {"start": v(61846.23, 4572) * mm, "end": v(61846.23, 304.8) * mm});
            skLineSegment(sketch, "E157.0.7", {"start": v(61846.23, 304.8) * mm, "end": v(80743.83, 304.8) * mm, "construction": true});
            skLineSegment(sketch, "E157.0.8", {"start": v(80743.83, 304.8) * mm, "end": v(80743.83, 3048) * mm});
            skLineSegment(sketch, "E158.bottom", {"start": v(78915.03, 2286) * mm, "end": v(79829.43, 2286) * mm, "construction": true});
            skLineSegment(sketch, "E158.top", {"start": v(78915.03, 304.8) * mm, "end": v(79829.43, 304.8) * mm, "construction": true});
            skLineSegment(sketch, "E158.left", {"start": v(78915.03, 2286) * mm, "end": v(78915.03, 304.8) * mm, "construction": true});
            skLineSegment(sketch, "E158.right", {"start": v(79829.43, 2286) * mm, "end": v(79829.43, 304.8) * mm, "construction": true});
            skLineSegment(sketch, "E159.bottom", {"start": v(74203.33, 2286) * mm, "end": v(76235.33, 2286) * mm, "construction": true});
            skLineSegment(sketch, "E159.top", {"start": v(74203.33, 304.8) * mm, "end": v(76235.33, 304.8) * mm, "construction": true});
            skLineSegment(sketch, "E159.left", {"start": v(74203.33, 2286) * mm, "end": v(74203.33, 304.8) * mm, "construction": true});
            skLineSegment(sketch, "E159.right", {"start": v(76235.33, 2286) * mm, "end": v(76235.33, 304.8) * mm, "construction": true});
            skLineSegment(sketch, "E160.bottom", {"start": v(70647.33, 2286) * mm, "end": v(72679.33, 2286) * mm, "construction": true});
            skLineSegment(sketch, "E160.top", {"start": v(70647.33, 304.8) * mm, "end": v(72679.33, 304.8) * mm, "construction": true});
            skLineSegment(sketch, "E160.left", {"start": v(70647.33, 2286) * mm, "end": v(70647.33, 304.8) * mm, "construction": true});
            skLineSegment(sketch, "E160.right", {"start": v(72679.33, 2286) * mm, "end": v(72679.33, 304.8) * mm, "construction": true});
            skLineSegment(sketch, "E161.bottom", {"start": v(63522.63, 3352.8) * mm, "end": v(66570.63, 3352.8) * mm});
            skLineSegment(sketch, "E161.top", {"start": v(63522.63, 304.8) * mm, "end": v(66570.63, 304.8) * mm});
            skLineSegment(sketch, "E161.left", {"start": v(63522.63, 3352.8) * mm, "end": v(63522.63, 304.8) * mm});
            skLineSegment(sketch, "E161.right", {"start": v(66570.63, 3352.8) * mm, "end": v(66570.63, 304.8) * mm});
            skLineSegment(sketch, "E162", {"start": v(68094.63, 4572) * mm, "end": v(68094.63, 304.8) * mm, "construction": true});
            skLineSegment(sketch, "E163", {"start": v(68208.93, 4572) * mm, "end": v(68208.93, 304.8) * mm, "construction": true});
            skLineSegment(sketch, "E164", {"start": v(61998.63, 304.8) * mm, "end": v(61998.63, 4572) * mm, "construction": true});
            skLineSegment(sketch, "E165", {"start": v(63522.63, 3352.8) * mm, "end": v(61998.63, 3352.8) * mm, "construction": true});
            skLineSegment(sketch, "E166", {"start": v(66570.63, 3352.8) * mm, "end": v(68094.63, 3352.8) * mm, "construction": true});
            skPoint(sketch, "E167", {"position": v(79372.23, 2286) * mm});
            skLineSegment(sketch, "E168.bottom", {"start": v(79042.03, 2133.6) * mm, "end": v(79308.73, 2133.6) * mm, "construction": true});
            skLineSegment(sketch, "E168.top", {"start": v(79042.03, 1879.6) * mm, "end": v(79308.73, 1879.6) * mm, "construction": true});
            skLineSegment(sketch, "E168.left", {"start": v(79042.03, 2133.6) * mm, "end": v(79042.03, 1879.6) * mm, "construction": true});
            skLineSegment(sketch, "E168.right", {"start": v(79308.73, 2133.6) * mm, "end": v(79308.73, 1879.6) * mm, "construction": true});
            skLineSegment(sketch, "E169.bottom", {"start": v(79435.73, 2133.6) * mm, "end": v(79702.43, 2133.6) * mm, "construction": true});
            skLineSegment(sketch, "E169.top", {"start": v(79435.73, 1879.6) * mm, "end": v(79702.43, 1879.6) * mm, "construction": true});
            skLineSegment(sketch, "E169.left", {"start": v(79435.73, 2133.6) * mm, "end": v(79435.73, 1879.6) * mm, "construction": true});
            skLineSegment(sketch, "E169.right", {"start": v(79702.43, 2133.6) * mm, "end": v(79702.43, 1879.6) * mm, "construction": true});
            skLineSegment(sketch, "E170.bottom", {"start": v(79042.03, 1727.2) * mm, "end": v(79308.73, 1727.2) * mm, "construction": true});
            skLineSegment(sketch, "E170.top", {"start": v(79042.03, 1244.6) * mm, "end": v(79308.73, 1244.6) * mm, "construction": true});
            skLineSegment(sketch, "E170.left", {"start": v(79042.03, 1727.2) * mm, "end": v(79042.03, 1244.6) * mm, "construction": true});
            skLineSegment(sketch, "E170.right", {"start": v(79308.73, 1727.2) * mm, "end": v(79308.73, 1244.6) * mm, "construction": true});
            skLineSegment(sketch, "E171.bottom", {"start": v(79435.73, 1727.2) * mm, "end": v(79702.43, 1727.2) * mm, "construction": true});
            skLineSegment(sketch, "E171.top", {"start": v(79435.73, 1244.6) * mm, "end": v(79702.43, 1244.6) * mm, "construction": true});
            skLineSegment(sketch, "E171.left", {"start": v(79435.73, 1727.2) * mm, "end": v(79435.73, 1244.6) * mm, "construction": true});
            skLineSegment(sketch, "E171.right", {"start": v(79702.43, 1727.2) * mm, "end": v(79702.43, 1244.6) * mm, "construction": true});
            skLineSegment(sketch, "E172.bottom", {"start": v(79042.03, 1041.4) * mm, "end": v(79308.73, 1041.4) * mm, "construction": true});
            skLineSegment(sketch, "E172.top", {"start": v(79042.03, 558.8) * mm, "end": v(79308.73, 558.8) * mm, "construction": true});
            skLineSegment(sketch, "E172.left", {"start": v(79042.03, 1041.4) * mm, "end": v(79042.03, 558.8) * mm, "construction": true});
            skLineSegment(sketch, "E172.right", {"start": v(79308.73, 1041.4) * mm, "end": v(79308.73, 558.8) * mm, "construction": true});
            skLineSegment(sketch, "E173.bottom", {"start": v(79435.73, 1041.4) * mm, "end": v(79702.43, 1041.4) * mm, "construction": true});
            skLineSegment(sketch, "E173.top", {"start": v(79435.73, 558.8) * mm, "end": v(79702.43, 558.8) * mm, "construction": true});
            skLineSegment(sketch, "E173.left", {"start": v(79435.73, 1041.4) * mm, "end": v(79435.73, 558.8) * mm, "construction": true});
            skLineSegment(sketch, "E173.right", {"start": v(79702.43, 1041.4) * mm, "end": v(79702.43, 558.8) * mm, "construction": true});
            skLineSegment(sketch, "E174", {"start": v(69123.33, 4572) * mm, "end": v(69123.33, 304.8) * mm, "construction": true});
            skLineSegment(sketch, "E175", {"start": v(78953.13, 4572) * mm, "end": v(78953.13, 304.8) * mm, "construction": true});
            skLineSegment(sketch, "E176", {"start": v(78038.73, 4572) * mm, "end": v(78038.73, 304.8) * mm, "construction": true});
            skLineSegment(sketch, "E177", {"start": v(68208.93, 3352.8) * mm, "end": v(80743.83, 3352.8) * mm, "construction": true});
            skLineSegment(sketch, "E178.bottom", {"start": v(70139.33, 2743.2) * mm, "end": v(73187.33, 2743.2) * mm});
            skLineSegment(sketch, "E178.top", {"start": v(70139.33, 304.8) * mm, "end": v(73187.33, 304.8) * mm});
            skLineSegment(sketch, "E178.left", {"start": v(70139.33, 2743.2) * mm, "end": v(70139.33, 304.8) * mm});
            skLineSegment(sketch, "E178.right", {"start": v(73187.33, 2743.2) * mm, "end": v(73187.33, 304.8) * mm});
            skLineSegment(sketch, "E179.bottom", {"start": v(73695.33, 2743.2) * mm, "end": v(76743.33, 2743.2) * mm});
            skLineSegment(sketch, "E179.top", {"start": v(73695.33, 304.8) * mm, "end": v(76743.33, 304.8) * mm});
            skLineSegment(sketch, "E179.left", {"start": v(73695.33, 2743.2) * mm, "end": v(73695.33, 304.8) * mm});
            skLineSegment(sketch, "E179.right", {"start": v(76743.33, 2743.2) * mm, "end": v(76743.33, 304.8) * mm});
            skLineSegment(sketch, "E180", {"start": v(71663.33, 2286) * mm, "end": v(71663.33, 2743.2) * mm, "construction": true});
            skLineSegment(sketch, "E181", {"start": v(75219.33, 2286) * mm, "end": v(75219.33, 2743.2) * mm, "construction": true});
            skLineSegment(sketch, "E182.bottom", {"start": v(77251.33, 304.8) * mm, "end": v(79689.73, 304.8) * mm});
            skLineSegment(sketch, "E182.top", {"start": v(77251.33, 2438.4) * mm, "end": v(79689.73, 2438.4) * mm});
            skLineSegment(sketch, "E182.left", {"start": v(77251.33, 304.8) * mm, "end": v(77251.33, 2438.4) * mm});
            skLineSegment(sketch, "E182.right", {"start": v(79689.73, 304.8) * mm, "end": v(79689.73, 2438.4) * mm});
            skSolve(sketch);
        }
        {
            var Q0;
            Q0=makeQuery(id+"F30.imprint","IMPRINT",FACE,{"disambiguationData":[TD([[makeQuery(id+"F30.imprint","IMPRINT",EDGE,{"derivedFrom":sQuery(id+"F30.wireOp",EDGE,"E161.bottom")}),-1.0]])]});
            var Q1;
            Q1=makeQuery(id+"F30.imprint","IMPRINT",FACE,{"disambiguationData":[TD([[makeQuery(id+"F30.imprint","IMPRINT",EDGE,{"derivedFrom":sQuery(id+"F30.wireOp",EDGE,"E178.bottom")}),-1.0]])]});
            var Q2;
            Q2=makeQuery(id+"F30.imprint","IMPRINT",FACE,{"disambiguationData":[TD([[makeQuery(id+"F30.imprint","IMPRINT",EDGE,{"derivedFrom":sQuery(id+"F30.wireOp",EDGE,"E179.bottom")}),-1.0]])]});
            var Q3;
            Q3=makeQuery(id+"F30.imprint","IMPRINT",FACE,{"disambiguationData":[TD([[makeQuery(id+"F30.imprint","IMPRINT",EDGE,{"derivedFrom":sQuery(id+"F30.wireOp",EDGE,"E182.bottom")}),-1.0]])]});
            extrude(context, id + "F31", {"entities" : qUnion([Q0, Q1, Q2, Q3]), "operationType" : NewBodyOperationType.REMOVE, "oppositeDirection" : true, "depth" : 50.8 * mm, "offsetDistance" : 25.4 * mm});
        }
    });
